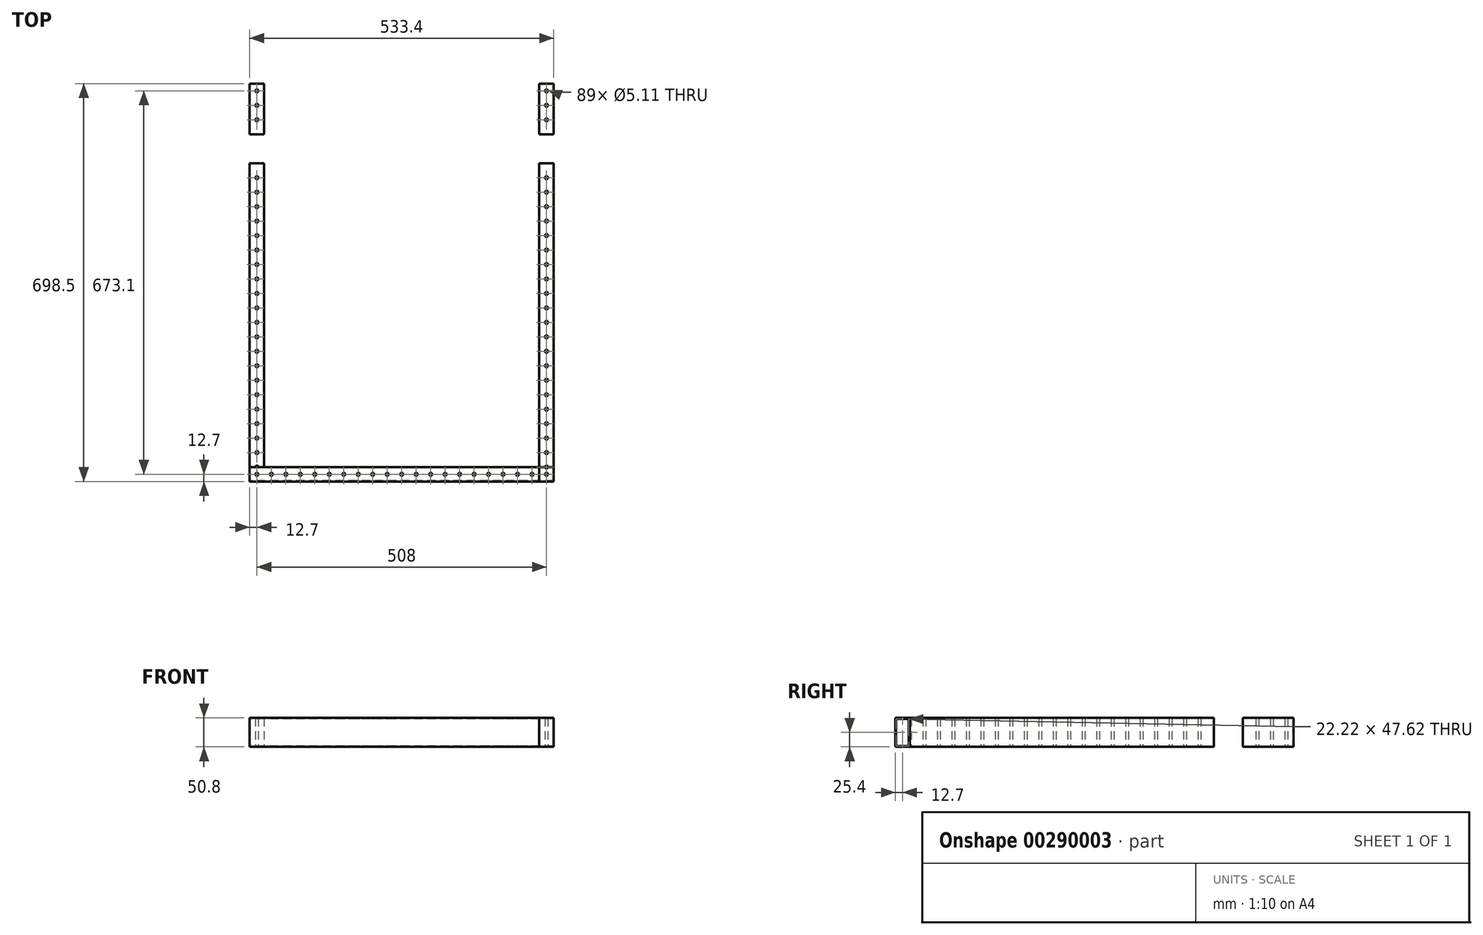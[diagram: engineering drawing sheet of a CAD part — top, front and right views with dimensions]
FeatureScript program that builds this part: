
annotation { "Feature Type Name" : "Feature", "Feature Type Description" : "" }
export const myFeature = defineFeature(function(context is Context, id is Id, definition is map)
    precondition{}
    {
        {
            var Q0;
            Q0=qCreatedBy(makeId("Top.planeOp"),FACE);
            var sketch = newSketch(context, id + "F0", { "sketchPlane" : qUnion([Q0])});
            skLineSegment(sketch, "E0", {"start": v(-266.7, 647.7) * mm, "end": v(-241.3, 647.7) * mm});
            skLineSegment(sketch, "E1", {"start": v(-241.3, 647.7) * mm, "end": v(-241.3, 558.8) * mm});
            skLineSegment(sketch, "E2", {"start": v(-241.3, 558.8) * mm, "end": v(-266.7, 558.8) * mm});
            skLineSegment(sketch, "E3", {"start": v(-266.7, 558.8) * mm, "end": v(-266.7, 647.7) * mm});
            skLineSegment(sketch, "E4", {"start": v(-266.7, 508) * mm, "end": v(-266.7, -25.4) * mm});
            skLineSegment(sketch, "E5", {"start": v(266.7, -50.8) * mm, "end": v(266.7, 508) * mm});
            skLineSegment(sketch, "E6", {"start": v(266.7, 508) * mm, "end": v(241.3, 508) * mm});
            skLineSegment(sketch, "E7", {"start": v(241.3, 508) * mm, "end": v(241.3, -50.8) * mm});
            skLineSegment(sketch, "E8", {"start": v(-241.3, -25.4) * mm, "end": v(-241.3, 508) * mm});
            skLineSegment(sketch, "E9", {"start": v(-241.3, 508) * mm, "end": v(-266.7, 508) * mm});
            skLineSegment(sketch, "E10", {"start": v(241.3, 558.8) * mm, "end": v(241.3, 647.7) * mm});
            skLineSegment(sketch, "E11", {"start": v(241.3, 647.7) * mm, "end": v(266.7, 647.7) * mm});
            skLineSegment(sketch, "E12", {"start": v(266.7, 647.7) * mm, "end": v(266.7, 558.8) * mm});
            skLineSegment(sketch, "E13", {"start": v(266.7, 558.8) * mm, "end": v(241.3, 558.8) * mm});
            skLineSegment(sketch, "E14", {"start": v(-266.7, -25.4) * mm, "end": v(-241.3, -25.4) * mm});
            skLineSegment(sketch, "E15", {"start": v(241.3, -50.8) * mm, "end": v(266.7, -50.8) * mm});
            skLineSegment(sketch, "E16.bottom", {"start": v(-241.3, -25.4) * mm, "end": v(241.3, -25.4) * mm});
            skLineSegment(sketch, "E16.top", {"start": v(-241.3, 0) * mm, "end": v(241.3, 0) * mm});
            skLineSegment(sketch, "E16.left", {"start": v(-241.3, -25.4) * mm, "end": v(-241.3, 0) * mm});
            skLineSegment(sketch, "E16.right", {"start": v(241.3, -25.4) * mm, "end": v(241.3, 0) * mm});
            skCircle(sketch, "E17", {"center": v(-254, 635) * mm, "radius": 2.55 * mm});
            skCircle(sketch, "E18.0.1.0", {"center": v(-254, 609.6) * mm, "radius": 2.55 * mm});
            skCircle(sketch, "E18.0.2.0", {"center": v(-254, 584.2) * mm, "radius": 2.55 * mm});
            skCircle(sketch, "E18.0.3.0", {"center": v(-254, 558.8) * mm, "radius": 2.55 * mm, "construction": true});
            skCircle(sketch, "E18.0.4.0", {"center": v(-254, 533.4) * mm, "radius": 2.55 * mm, "construction": true});
            skCircle(sketch, "E18.0.5.0", {"center": v(-254, 508) * mm, "radius": 2.55 * mm, "construction": true});
            skCircle(sketch, "E18.0.6.0", {"center": v(-254, 482.6) * mm, "radius": 2.55 * mm});
            skCircle(sketch, "E18.0.7.0", {"center": v(-254, 457.2) * mm, "radius": 2.55 * mm});
            skCircle(sketch, "E18.0.8.0", {"center": v(-254, 431.8) * mm, "radius": 2.55 * mm});
            skCircle(sketch, "E18.0.9.0", {"center": v(-254, 406.4) * mm, "radius": 2.55 * mm});
            skCircle(sketch, "E18.0.10.0", {"center": v(-254, 381) * mm, "radius": 2.55 * mm});
            skCircle(sketch, "E18.0.11.0", {"center": v(-254, 355.6) * mm, "radius": 2.55 * mm});
            skCircle(sketch, "E18.0.12.0", {"center": v(-254, 330.2) * mm, "radius": 2.55 * mm});
            skCircle(sketch, "E18.0.13.0", {"center": v(-254, 304.8) * mm, "radius": 2.55 * mm});
            skCircle(sketch, "E18.0.14.0", {"center": v(-254, 279.4) * mm, "radius": 2.55 * mm});
            skCircle(sketch, "E18.0.15.0", {"center": v(-254, 254) * mm, "radius": 2.55 * mm});
            skCircle(sketch, "E18.0.16.0", {"center": v(-254, 228.6) * mm, "radius": 2.55 * mm});
            skCircle(sketch, "E18.0.17.0", {"center": v(-254, 203.2) * mm, "radius": 2.55 * mm});
            skCircle(sketch, "E18.0.18.0", {"center": v(-254, 177.8) * mm, "radius": 2.55 * mm});
            skCircle(sketch, "E18.0.19.0", {"center": v(-254, 152.4) * mm, "radius": 2.55 * mm});
            skCircle(sketch, "E18.0.20.0", {"center": v(-254, 127) * mm, "radius": 2.55 * mm});
            skCircle(sketch, "E18.0.21.0", {"center": v(-254, 101.6) * mm, "radius": 2.55 * mm});
            skCircle(sketch, "E18.0.22.0", {"center": v(-254, 76.2) * mm, "radius": 2.55 * mm});
            skCircle(sketch, "E18.0.23.0", {"center": v(-254, 50.8) * mm, "radius": 2.55 * mm});
            skCircle(sketch, "E18.0.24.0", {"center": v(-254, 25.4) * mm, "radius": 2.55 * mm});
            skCircle(sketch, "E18.0.25.0", {"center": v(-254, 0) * mm, "radius": 2.55 * mm});
            skCircle(sketch, "E18.0.26.0", {"center": v(-254, -25.4) * mm, "radius": 2.55 * mm});
            skCircle(sketch, "E18.1.0.0", {"center": v(254, 635) * mm, "radius": 2.55 * mm});
            skCircle(sketch, "E18.1.1.0", {"center": v(254, 609.6) * mm, "radius": 2.55 * mm});
            skCircle(sketch, "E18.1.2.0", {"center": v(254, 584.2) * mm, "radius": 2.55 * mm});
            skCircle(sketch, "E18.1.3.0", {"center": v(254, 558.8) * mm, "radius": 2.55 * mm, "construction": true});
            skCircle(sketch, "E18.1.4.0", {"center": v(254, 533.4) * mm, "radius": 2.55 * mm, "construction": true});
            skCircle(sketch, "E18.1.5.0", {"center": v(254, 508) * mm, "radius": 2.55 * mm, "construction": true});
            skCircle(sketch, "E18.1.6.0", {"center": v(254, 482.6) * mm, "radius": 2.55 * mm});
            skCircle(sketch, "E18.1.7.0", {"center": v(254, 457.2) * mm, "radius": 2.55 * mm});
            skCircle(sketch, "E18.1.8.0", {"center": v(254, 431.8) * mm, "radius": 2.55 * mm});
            skCircle(sketch, "E18.1.9.0", {"center": v(254, 406.4) * mm, "radius": 2.55 * mm});
            skCircle(sketch, "E18.1.10.0", {"center": v(254, 381) * mm, "radius": 2.55 * mm});
            skCircle(sketch, "E18.1.11.0", {"center": v(254, 355.6) * mm, "radius": 2.55 * mm});
            skCircle(sketch, "E18.1.12.0", {"center": v(254, 330.2) * mm, "radius": 2.55 * mm});
            skCircle(sketch, "E18.1.13.0", {"center": v(254, 304.8) * mm, "radius": 2.55 * mm});
            skCircle(sketch, "E18.1.14.0", {"center": v(254, 279.4) * mm, "radius": 2.55 * mm});
            skCircle(sketch, "E18.1.15.0", {"center": v(254, 254) * mm, "radius": 2.55 * mm});
            skCircle(sketch, "E18.1.16.0", {"center": v(254, 228.6) * mm, "radius": 2.55 * mm});
            skCircle(sketch, "E18.1.17.0", {"center": v(254, 203.2) * mm, "radius": 2.55 * mm});
            skCircle(sketch, "E18.1.18.0", {"center": v(254, 177.8) * mm, "radius": 2.55 * mm});
            skCircle(sketch, "E18.1.19.0", {"center": v(254, 152.4) * mm, "radius": 2.55 * mm});
            skCircle(sketch, "E18.1.20.0", {"center": v(254, 127) * mm, "radius": 2.55 * mm});
            skCircle(sketch, "E18.1.21.0", {"center": v(254, 101.6) * mm, "radius": 2.55 * mm});
            skCircle(sketch, "E18.1.22.0", {"center": v(254, 76.2) * mm, "radius": 2.55 * mm});
            skCircle(sketch, "E18.1.23.0", {"center": v(254, 50.8) * mm, "radius": 2.55 * mm});
            skCircle(sketch, "E18.1.24.0", {"center": v(254, 25.4) * mm, "radius": 2.55 * mm});
            skCircle(sketch, "E18.1.25.0", {"center": v(254, 0) * mm, "radius": 2.55 * mm});
            skCircle(sketch, "E18.1.26.0", {"center": v(254, -25.4) * mm, "radius": 2.55 * mm});
            skLineSegment(sketch, "E18.direction1", {"start": v(-254, 635) * mm, "end": v(254, 635) * mm, "construction": true});
            skLineSegment(sketch, "E18.direction2", {"start": v(-254, 635) * mm, "end": v(-254, 609.6) * mm, "construction": true});
            skCircle(sketch, "E19", {"center": v(-228.6, -12.7) * mm, "radius": 2.55 * mm});
            skPoint(sketch, "E19.centerSnap0", {"position": v(-241.3, -12.7) * mm});
            skCircle(sketch, "E20.1.0.0", {"center": v(-203.2, -12.7) * mm, "radius": 2.55 * mm});
            skCircle(sketch, "E20.2.0.0", {"center": v(-177.8, -12.7) * mm, "radius": 2.55 * mm});
            skCircle(sketch, "E20.3.0.0", {"center": v(-152.4, -12.7) * mm, "radius": 2.55 * mm});
            skCircle(sketch, "E20.4.0.0", {"center": v(-127, -12.7) * mm, "radius": 2.55 * mm});
            skCircle(sketch, "E20.5.0.0", {"center": v(-101.6, -12.7) * mm, "radius": 2.55 * mm});
            skCircle(sketch, "E20.6.0.0", {"center": v(-76.2, -12.7) * mm, "radius": 2.55 * mm});
            skCircle(sketch, "E20.7.0.0", {"center": v(-50.8, -12.7) * mm, "radius": 2.55 * mm});
            skCircle(sketch, "E20.8.0.0", {"center": v(-25.4, -12.7) * mm, "radius": 2.55 * mm});
            skCircle(sketch, "E20.9.0.0", {"center": v(0, -12.7) * mm, "radius": 2.55 * mm});
            skCircle(sketch, "E20.10.0.0", {"center": v(25.4, -12.7) * mm, "radius": 2.55 * mm});
            skCircle(sketch, "E20.11.0.0", {"center": v(50.8, -12.7) * mm, "radius": 2.55 * mm});
            skCircle(sketch, "E20.12.0.0", {"center": v(76.2, -12.7) * mm, "radius": 2.55 * mm});
            skCircle(sketch, "E20.13.0.0", {"center": v(101.6, -12.7) * mm, "radius": 2.55 * mm});
            skCircle(sketch, "E20.14.0.0", {"center": v(127, -12.7) * mm, "radius": 2.55 * mm});
            skCircle(sketch, "E20.15.0.0", {"center": v(152.4, -12.7) * mm, "radius": 2.55 * mm});
            skCircle(sketch, "E20.16.0.0", {"center": v(177.8, -12.7) * mm, "radius": 2.55 * mm});
            skCircle(sketch, "E20.17.0.0", {"center": v(203.2, -12.7) * mm, "radius": 2.55 * mm});
            skCircle(sketch, "E20.18.0.0", {"center": v(228.6, -12.7) * mm, "radius": 2.55 * mm});
            skLineSegment(sketch, "E20.direction1", {"start": v(-228.6, -12.7) * mm, "end": v(-203.2, -12.7) * mm, "construction": true});
            skSolve(sketch);
        }
        {
            var Q0;
            Q0=makeQuery(id+"F0.imprint","IMPRINT",FACE,{"disambiguationData":[TD([[makeQuery(id+"F0.imprint","IMPRINT",EDGE,{"derivedFrom":sQuery(id+"F0.wireOp",EDGE,"E4")}),1.0]])]});
            var Q1;
            Q1=makeQuery(id+"F0.imprint","IMPRINT",FACE,{"disambiguationData":[TD([[makeQuery(id+"F0.imprint","IMPRINT",EDGE,{"derivedFrom":sQuery(id+"F0.wireOp",EDGE,"E0")}),-1.0]])]});
            var Q2;
            Q2=makeQuery(id+"F0.imprint","IMPRINT",FACE,{"disambiguationData":[TD([[makeQuery(id+"F0.imprint","IMPRINT",EDGE,{"derivedFrom":sQuery(id+"F0.wireOp",EDGE,"E5")}),1.0]])]});
            var Q3;
            Q3=makeQuery(id+"F0.imprint","IMPRINT",FACE,{"disambiguationData":[TD([[makeQuery(id+"F0.imprint","IMPRINT",EDGE,{"derivedFrom":sQuery(id+"F0.wireOp",EDGE,"E10")}),-1.0]])]});
            extrude(context, id + "F1", {"entities" : qUnion([Q0, Q1, Q2, Q3]), "depth" : 50.8 * mm});
        }
        {
            var Q0;
            Q0=makeQuery(id+"F1.opExtrude","SWEPT_FACE",FACE,{"disambiguationData":[OSD([sQuery(id+"F0.wireOp",EDGE,"E4")])]});
            var sketch = newSketch(context, id + "F2", { "sketchPlane" : qUnion([Q0])});
            skLineSegment(sketch, "E21.bottom", {"start": v(25.4, 50.8) * mm, "end": v(50.8, 50.8) * mm});
            skLineSegment(sketch, "E21.top", {"start": v(25.4, 0) * mm, "end": v(50.8, 0) * mm});
            skLineSegment(sketch, "E21.left", {"start": v(25.4, 50.8) * mm, "end": v(25.4, 0) * mm});
            skLineSegment(sketch, "E21.right", {"start": v(50.8, 50.8) * mm, "end": v(50.8, 0) * mm});
            skLineSegment(sketch, "E22.bottom", {"start": v(49.21, 49.21) * mm, "end": v(26.99, 49.21) * mm});
            skLineSegment(sketch, "E22.top", {"start": v(49.21, 1.59) * mm, "end": v(26.99, 1.59) * mm});
            skLineSegment(sketch, "E22.left", {"start": v(49.21, 49.21) * mm, "end": v(49.21, 1.59) * mm});
            skLineSegment(sketch, "E22.right", {"start": v(26.99, 49.21) * mm, "end": v(26.99, 1.59) * mm});
            skPoint(sketch, "E22.middle", {"position": v(38.1, 25.4) * mm});
            skPoint(sketch, "E22.middle.positionSnap0", {"position": v(25.4, 25.4) * mm});
            skPoint(sketch, "E22.centerSnap0", {"position": v(25.4, 25.4) * mm});
            skSolve(sketch);
        }
        {
            var Q0;
            Q0=makeQuery(id+"F2.imprint","IMPRINT",FACE,{"disambiguationData":[TD([[makeQuery(id+"F2.imprint","IMPRINT",EDGE,{"derivedFrom":sQuery(id+"F2.wireOp",EDGE,"E21.bottom")}),-1.0]])]});
            var Q1;
            Q1=makeQuery(id+"F1.opExtrude","SWEPT_FACE",FACE,{"disambiguationData":[OSD([sQuery(id+"F0.wireOp",EDGE,"E5")])]});
            extrude(context, id + "F3", {"entities" : qUnion([Q0]), "endBound" : BoundingType.UP_TO_SURFACE, "oppositeDirection" : true, "endBoundEntityFace" : qUnion([Q1]), "depth" : 25.4 * mm});
        }
        {
            var Q0;
            Q0=makeQuery(id+"F3.opExtrude","SWEPT_FACE",FACE,{"disambiguationData":[OSD([sQuery(id+"F2.wireOp",EDGE,"E21.bottom")])]});
            var sketch = newSketch(context, id + "F4", { "sketchPlane" : qUnion([Q0])});
            skCircle(sketch, "E23", {"center": v(-254, -38.1) * mm, "radius": 2.55 * mm});
            skCircle(sketch, "E24.1.0.0", {"center": v(-228.6, -38.1) * mm, "radius": 2.55 * mm});
            skCircle(sketch, "E24.2.0.0", {"center": v(-203.2, -38.1) * mm, "radius": 2.55 * mm});
            skCircle(sketch, "E24.3.0.0", {"center": v(-177.8, -38.1) * mm, "radius": 2.55 * mm});
            skCircle(sketch, "E24.4.0.0", {"center": v(-152.4, -38.1) * mm, "radius": 2.55 * mm});
            skCircle(sketch, "E24.5.0.0", {"center": v(-127, -38.1) * mm, "radius": 2.55 * mm});
            skCircle(sketch, "E24.6.0.0", {"center": v(-101.6, -38.1) * mm, "radius": 2.55 * mm});
            skCircle(sketch, "E24.7.0.0", {"center": v(-76.2, -38.1) * mm, "radius": 2.55 * mm});
            skCircle(sketch, "E24.8.0.0", {"center": v(-50.8, -38.1) * mm, "radius": 2.55 * mm});
            skCircle(sketch, "E24.9.0.0", {"center": v(-25.4, -38.1) * mm, "radius": 2.55 * mm});
            skCircle(sketch, "E24.10.0.0", {"center": v(0, -38.1) * mm, "radius": 2.55 * mm});
            skCircle(sketch, "E24.11.0.0", {"center": v(25.4, -38.1) * mm, "radius": 2.55 * mm});
            skCircle(sketch, "E24.12.0.0", {"center": v(50.8, -38.1) * mm, "radius": 2.55 * mm});
            skCircle(sketch, "E24.13.0.0", {"center": v(76.2, -38.1) * mm, "radius": 2.55 * mm});
            skCircle(sketch, "E24.14.0.0", {"center": v(101.6, -38.1) * mm, "radius": 2.55 * mm});
            skCircle(sketch, "E24.15.0.0", {"center": v(127, -38.1) * mm, "radius": 2.55 * mm});
            skCircle(sketch, "E24.16.0.0", {"center": v(152.4, -38.1) * mm, "radius": 2.55 * mm});
            skCircle(sketch, "E24.17.0.0", {"center": v(177.8, -38.1) * mm, "radius": 2.55 * mm});
            skCircle(sketch, "E24.18.0.0", {"center": v(203.2, -38.1) * mm, "radius": 2.55 * mm});
            skCircle(sketch, "E24.19.0.0", {"center": v(228.6, -38.1) * mm, "radius": 2.55 * mm});
            skCircle(sketch, "E24.20.0.0", {"center": v(254, -38.1) * mm, "radius": 2.55 * mm});
            skLineSegment(sketch, "E24.direction1", {"start": v(-254, -38.1) * mm, "end": v(-228.6, -38.1) * mm, "construction": true});
            skSolve(sketch);
        }
        {
            var Q0;
            Q0=sQuery(id+"F4.wireOp",VERTEX,"E24.11.0.0.center");
            var Q1;
            Q1=sQuery(id+"F4.wireOp",VERTEX,"E24.12.0.0.center");
            var Q2;
            Q2=sQuery(id+"F4.wireOp",VERTEX,"E24.13.0.0.center");
            var Q3;
            Q3=sQuery(id+"F4.wireOp",VERTEX,"E24.1.0.0.center");
            var Q4;
            Q4=sQuery(id+"F4.wireOp",VERTEX,"E24.15.0.0.center");
            var Q5;
            Q5=sQuery(id+"F4.wireOp",VERTEX,"E24.2.0.0.center");
            var Q6;
            Q6=sQuery(id+"F4.wireOp",VERTEX,"E24.direction1.start");
            var Q7;
            Q7=sQuery(id+"F4.wireOp",VERTEX,"E24.3.0.0.center");
            var Q8;
            Q8=sQuery(id+"F4.wireOp",VERTEX,"E24.4.0.0.center");
            var Q9;
            Q9=sQuery(id+"F4.wireOp",VERTEX,"E24.5.0.0.center");
            var Q10;
            Q10=sQuery(id+"F4.wireOp",VERTEX,"E24.6.0.0.center");
            var Q11;
            Q11=sQuery(id+"F4.wireOp",VERTEX,"E24.7.0.0.center");
            var Q12;
            Q12=sQuery(id+"F4.wireOp",VERTEX,"E24.8.0.0.center");
            var Q13;
            Q13=sQuery(id+"F4.wireOp",VERTEX,"E24.9.0.0.center");
            var Q14;
            Q14=sQuery(id+"F4.wireOp",VERTEX,"E24.10.0.0.center");
            var Q15;
            Q15=sQuery(id+"F4.wireOp",VERTEX,"E24.20.0.0.center");
            var Q16;
            Q16=sQuery(id+"F4.wireOp",VERTEX,"E24.18.0.0.center");
            var Q17;
            Q17=sQuery(id+"F4.wireOp",VERTEX,"E24.16.0.0.center");
            var Q18;
            Q18=sQuery(id+"F4.wireOp",VERTEX,"E24.14.0.0.center");
            var Q19;
            Q19=sQuery(id+"F4.wireOp",VERTEX,"E24.19.0.0.center");
            var Q20;
            Q20=sQuery(id+"F4.wireOp",VERTEX,"E24.17.0.0.center");
            var Q21;
            Q21=makeQuery(id+"F3.opExtrude","SWEPT_BODY",BODY,{"disambiguationData":[OSD([sQuery(id+"F2.wireOp",EDGE,"E21.bottom"),sQuery(id+"F2.wireOp",EDGE,"E21.top"),sQuery(id+"F2.wireOp",EDGE,"E21.left"),sQuery(id+"F2.wireOp",EDGE,"E21.right"),sQuery(id+"F2.wireOp",EDGE,"E22.bottom"),sQuery(id+"F2.wireOp",EDGE,"E22.top"),sQuery(id+"F2.wireOp",EDGE,"E22.left"),sQuery(id+"F2.wireOp",EDGE,"E22.right")])]});
            hole(context, id + "F5", {"style" : HoleStyle.SIMPLE, "endStyle" : HoleEndStyle.THROUGH, "holeDiameter" : 5.1 * mm, "tappedDepth" : 12.7 * mm, "tapClearance" : 3, "locations" : qUnion([Q0, Q1, Q2, Q3, Q4, Q5, Q6, Q7, Q8, Q9, Q10, Q11, Q12, Q13, Q14, Q15, Q16, Q17, Q18, Q19, Q20]), "scope" : qUnion([Q21])});
        }
    });
